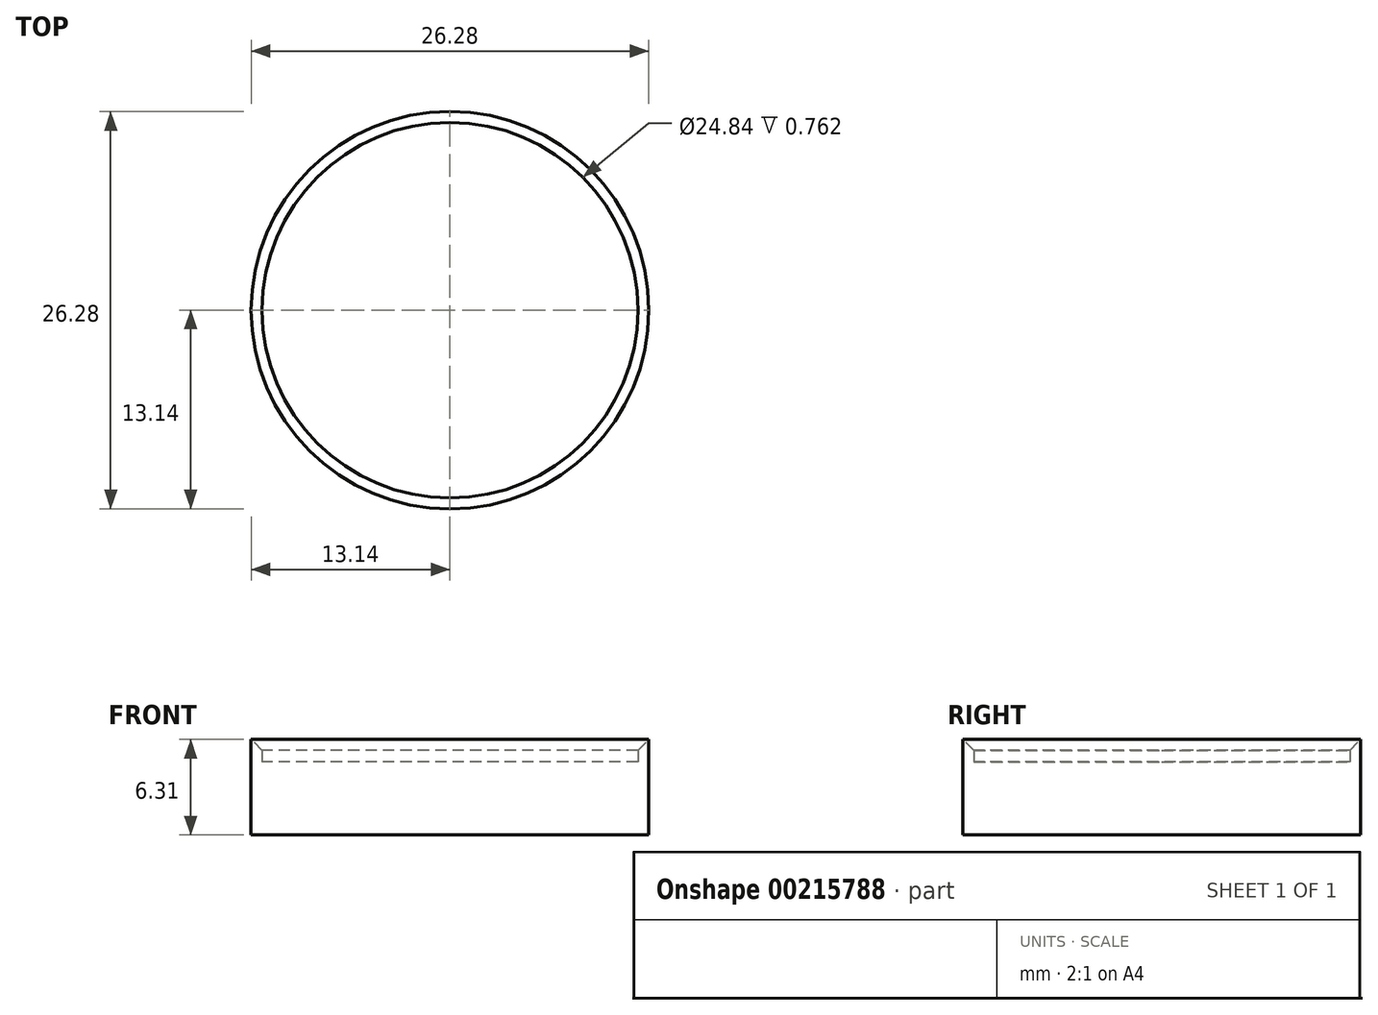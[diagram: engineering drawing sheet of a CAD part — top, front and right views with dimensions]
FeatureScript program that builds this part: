
annotation { "Feature Type Name" : "Feature", "Feature Type Description" : "" }
export const myFeature = defineFeature(function(context is Context, id is Id, definition is map)
    precondition{}
    {
        {
            var Q0;
            Q0=qCreatedBy(makeId("Top.planeOp"),FACE);
            var sketch = newSketch(context, id + "F0", { "sketchPlane" : qUnion([Q0])});
            skCircle(sketch, "E0", {"center": v(0, 0) * mm, "radius": 13.14 * mm});
            skSolve(sketch);
        }
        {
            var Q0;
            Q0=makeQuery(id+"F0.imprint","IMPRINT",FACE,{"disambiguationData":[TD([[makeQuery(id+"F0.imprint","IMPRINT",EDGE,{"derivedFrom":sQuery(id+"F0.wireOp",EDGE,"E0")}),1.0]])]});
            extrude(context, id + "F1", {"entities" : qUnion([Q0]), "depth" : 4.83 * mm});
        }
        {
            var Q0;
            Q0=makeQuery(id+"F1.opExtrude","CAP_FACE",FACE,{"disambiguationData":[OSD([sQuery(id+"F0.wireOp",EDGE,"E0")])],"isStart":false});
            var sketch = newSketch(context, id + "F2", { "sketchPlane" : qUnion([Q0])});
            skCircle(sketch, "E1", {"center": v(0, 0) * mm, "radius": 13.14 * mm});
            skCircle(sketch, "E2", {"center": v(0, 0) * mm, "radius": 12.42 * mm});
            skSolve(sketch);
        }
        {
            var Q0;
            Q0 = qSketchRegion(id + "F2", true);
            extrude(context, id + "F3", {"entities" : qUnion([Q0]), "operationType" : NewBodyOperationType.ADD, "depth" : 1.52 * mm});
        }
        {
            var Q0;
            Q0=makeQuery(id+"F3.opExtrude","CAP_EDGE",EDGE,{"disambiguationData":[OSD([sQuery(id+"F2.wireOp",EDGE,"E2")])],"isStart":false});
            chamfer(context, id + "F4", {"entities" : qUnion([Q0]), "width" : 0.76 * mm, "tangentPropagation" : true});
        }
    });
